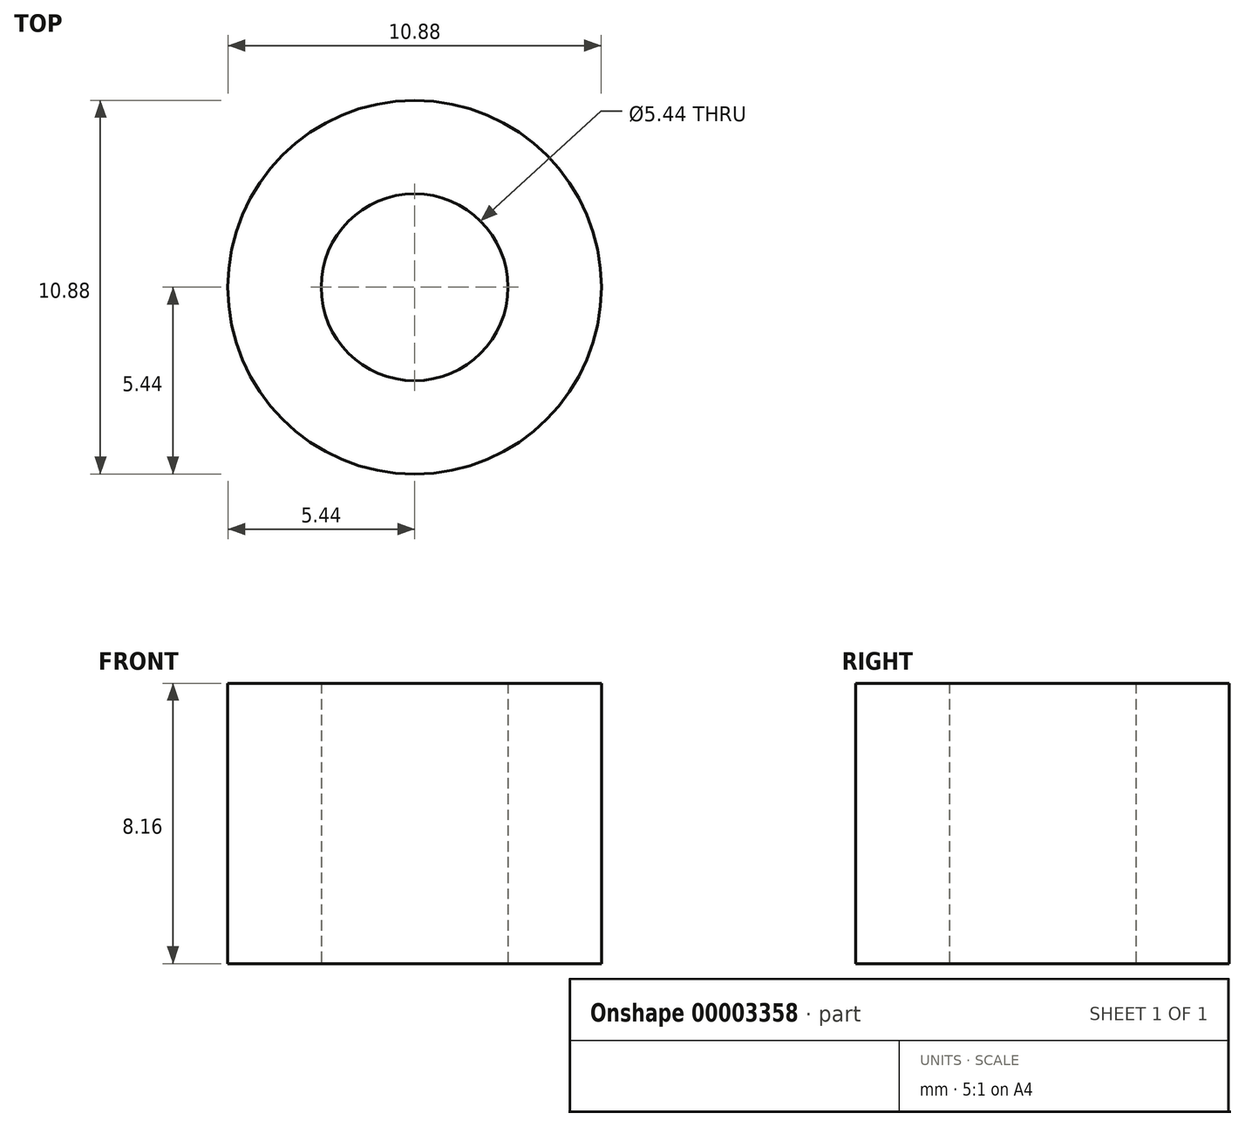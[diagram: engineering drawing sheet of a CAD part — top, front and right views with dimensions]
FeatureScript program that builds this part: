
annotation { "Feature Type Name" : "Feature", "Feature Type Description" : "" }
export const myFeature = defineFeature(function(context is Context, id is Id, definition is map)
    precondition{}
    {
        {
            var Q0;
            Q0=qCreatedBy(makeId("Top.planeOp"),FACE);
            var sketch = newSketch(context, id + "F0", { "sketchPlane" : qUnion([Q0])});
            skCircle(sketch, "E0", {"center": v(0, 0) * mm, "radius": 25.4 * mm});
            skCircle(sketch, "E1", {"center": v(0, 0) * mm, "radius": 12.7 * mm});
            skSolve(sketch);
        }
        {
            var Q0;
            Q0 = qSketchRegion(id + "F0", true);
            extrude(context, id + "F1", {"entities" : qUnion([Q0]), "depth" : 38.1 * mm});
        }
        {
            var Q0;
            Q0=makeQuery(id+"F1.opExtrude","SWEPT_BODY",BODY,{"disambiguationData":[OSD([sQuery(id+"F0.wireOp",EDGE,"E0"),sQuery(id+"F0.wireOp",EDGE,"E1")])]});
            var Q1;
            Q1=qCreatedBy(makeId("Origin.pointOp"),VERTEX);
            transform(context, id + "F2", {"entities" : qUnion([Q0]), "transformType" : TransformType.SCALE_UNIFORMLY, "scale" : 6 / 28, "makeCopy" : false, "scalePoint" : qUnion([Q1])});
        }
    });
